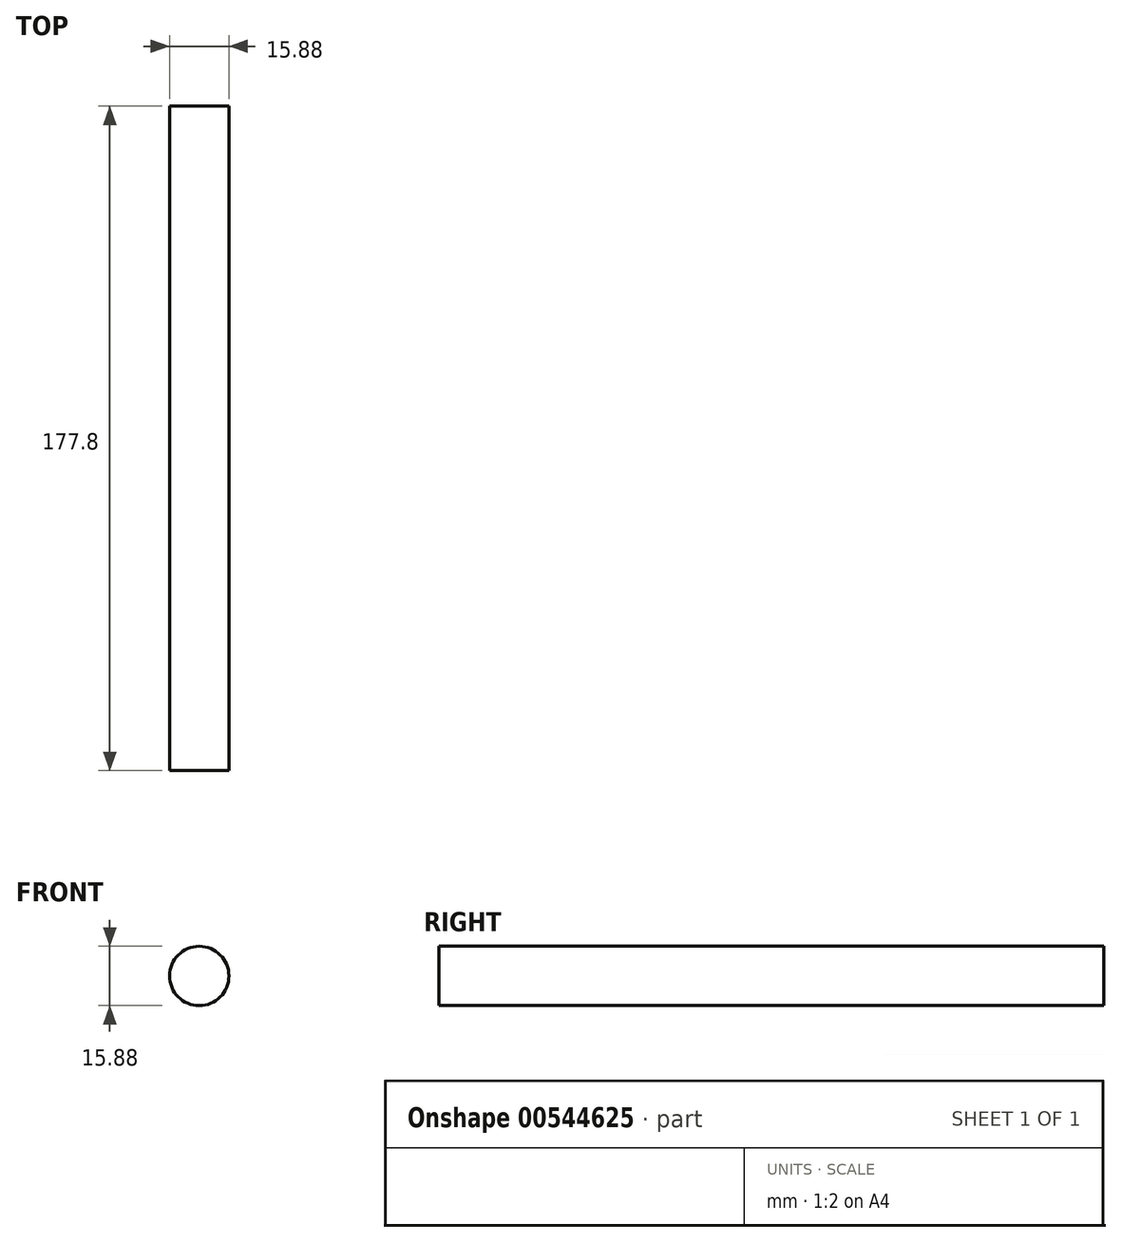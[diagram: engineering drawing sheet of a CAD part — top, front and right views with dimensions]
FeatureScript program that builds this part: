
annotation { "Feature Type Name" : "Feature", "Feature Type Description" : "" }
export const myFeature = defineFeature(function(context is Context, id is Id, definition is map)
    precondition{}
    {
        {
            var Q0;
            Q0=qCreatedBy(makeId("Front.planeOp"),FACE);
            var sketch = newSketch(context, id + "F0", { "sketchPlane" : qUnion([Q0])});
            skCircle(sketch, "E0", {"center": v(0, 0) * mm, "radius": 7.94 * mm});
            skSolve(sketch);
        }
        {
            var Q0;
            Q0 = qSketchRegion(id + "F0", true);
            extrude(context, id + "F1", {"entities" : qUnion([Q0]), "endBound" : BoundingType.SYMMETRIC, "depth" : 177.8 * mm, "offsetDistance" : 25.4 * mm});
        }
    });
